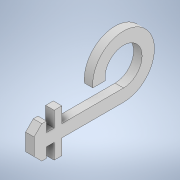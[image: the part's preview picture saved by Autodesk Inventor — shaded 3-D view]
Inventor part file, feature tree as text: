
AUTODESK INVENTOR PART (.ipt)
format: ipt  version: 2020 (Build 240168000, 168)  size: 131,584 bytes
history: native  units: mm
features: extrude x1, sketch x1
ambient origin geometry x8: Origin, YZ Plane, XZ Plane, XY Plane, X Axis, Y Axis, Z Axis, Center Point
bodies: Solide1 (feature_tree)
feature tree (2):
  extrude  "Extrusion1"  Depth=8.0mm
  sketch  "Esquisse1"
